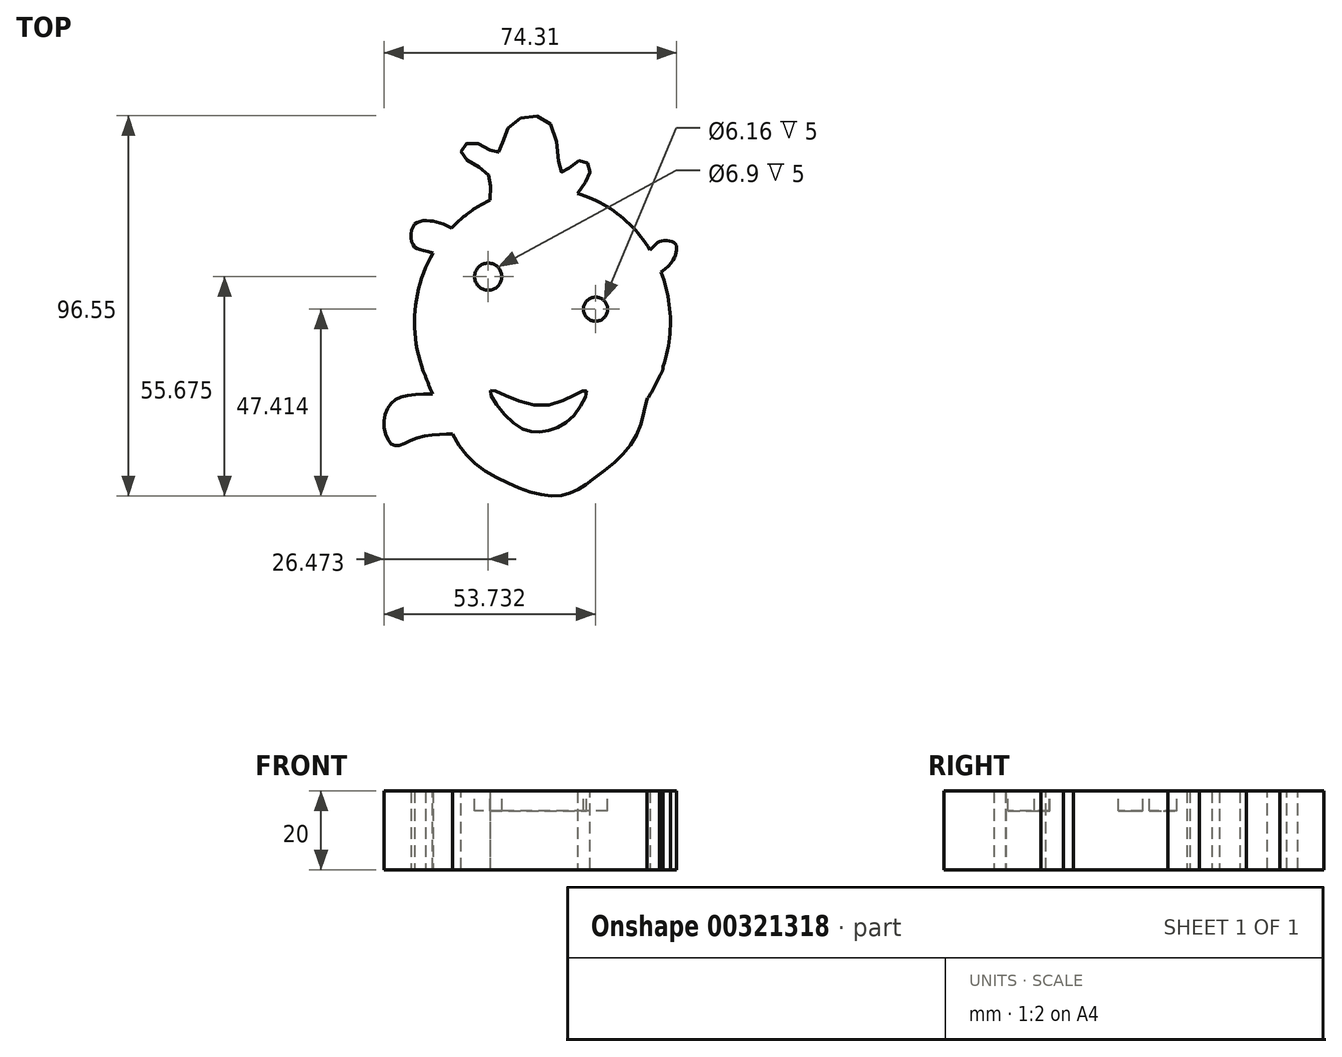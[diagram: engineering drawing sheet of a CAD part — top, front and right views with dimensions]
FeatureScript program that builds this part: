
annotation { "Feature Type Name" : "Feature", "Feature Type Description" : "" }
export const myFeature = defineFeature(function(context is Context, id is Id, definition is map)
    precondition{}
    {
        {
            var Q0;
            Q0=qCreatedBy(makeId("Top.planeOp"),FACE);
            var sketch = newSketch(context, id + "F0", { "sketchPlane" : qUnion([Q0])});
            skEllipse(sketch, "E0", {"center": v(0, 0) * mm, "majorRadius": 34 * mm, "minorRadius": 32.5 * mm, "majorAxis": v(0, -1)});
            skFitSpline(sketch, "E1", {"points": [v(-13.35, 31) * mm, v(-14.26, 38.11) * mm, v(-20.56, 42.77) * mm, v(-17.82, 45.8) * mm, v(-11.52, 43.05) * mm, v(-8.23, 49.9) * mm, v(1.92, 50.45) * mm, v(4.94, 38.11) * mm, v(9.6, 41.13) * mm, v(12.06, 38.94) * mm, v(8.85, 32.71) * mm], "startDerivative": vector(4.19, 88.84) * mm, "endDerivative": vector(-53.54, -70.88) * mm});
            skFitSpline(sketch, "E2", {"points": [v(-32.18, -4.76) * mm, v(-24.4, -25.5) * mm, v(-18.1, -35.1) * mm, v(-8.77, -40.85) * mm, v(0, -43.87) * mm, v(6.58, -43.6) * mm, v(11.52, -40.85) * mm, v(19.47, -34.55) * mm, v(24.68, -26.87) * mm, v(27.7, -16.73) * mm, v(30.68, -11.21) * mm], "startDerivative": vector(26.14, -156.38) * mm, "endDerivative": vector(-1.12, 73.73) * mm});
            skFitSpline(sketch, "E3", {"points": [v(-23.1, 23.92) * mm, v(-28.8, 25.77) * mm, v(-32.63, 24.68) * mm, v(-32.9, 19.74) * mm, v(-27.8, 17.6) * mm], "startDerivative": vector(-25.68, 14.25) * mm, "endDerivative": vector(31.45, -7.4) * mm});
            skFitSpline(sketch, "E4", {"points": [v(27.38, 18.32) * mm, v(29.96, 20.51) * mm, v(33.46, 20.24) * mm, v(34, 18.08) * mm, v(30.15, 12.7) * mm], "startDerivative": vector(16.16, 15.6) * mm, "endDerivative": vector(-25.33, -19.84) * mm});
            skFitSpline(sketch, "E5", {"points": [v(-27.93, -18.2) * mm, v(-37.78, -19.97) * mm, v(-40.21, -26.45) * mm, v(-37.78, -31.3) * mm, v(-32.18, -29.54) * mm, v(-22.86, -28.46) * mm], "startDerivative": vector(-53.4, -2.35) * mm, "endDerivative": vector(30.93, -1.17) * mm});
            skSolve(sketch);
        }
        {
            var Q0;
            Q0 = qSketchRegion(id + "F0", true);
            extrude(context, id + "F1", {"entities" : qUnion([Q0]), "depth" : 20 * mm});
        }
        {
            var Q0;
            Q0=makeQuery(id+"F1.opExtrude","CAP_FACE",FACE,{"disambiguationData":[OSD([sQuery(id+"F0.wireOp",EDGE,"E0"),sQuery(id+"F0.wireOp",EDGE,"E1"),sQuery(id+"F0.wireOp",EDGE,"E2"),sQuery(id+"F0.wireOp",EDGE,"E3"),sQuery(id+"F0.wireOp",EDGE,"E4"),sQuery(id+"F0.wireOp",EDGE,"E5")])],"isStart":false});
            var sketch = newSketch(context, id + "F2", { "sketchPlane" : qUnion([Q0])});
            skCircle(sketch, "E6", {"center": v(-13.77, 11.56) * mm, "radius": 3.45 * mm});
            skCircle(sketch, "E7", {"center": v(13.5, 3.3) * mm, "radius": 3.08 * mm});
            skFitSpline(sketch, "E8", {"points": [v(-13.22, -17.35) * mm, v(0, -21.2) * mm, v(11.01, -17.35) * mm, v(7.99, -23.68) * mm, v(0, -27.81) * mm, v(-7.7, -25.33) * mm, v(-13.22, -17.35) * mm]});
            skSolve(sketch);
        }
        {
            var Q0;
            Q0 = qSketchRegion(id + "F2", true);
            extrude(context, id + "F3", {"entities" : qUnion([Q0]), "operationType" : NewBodyOperationType.REMOVE, "oppositeDirection" : true, "depth" : 5 * mm});
        }
    });
